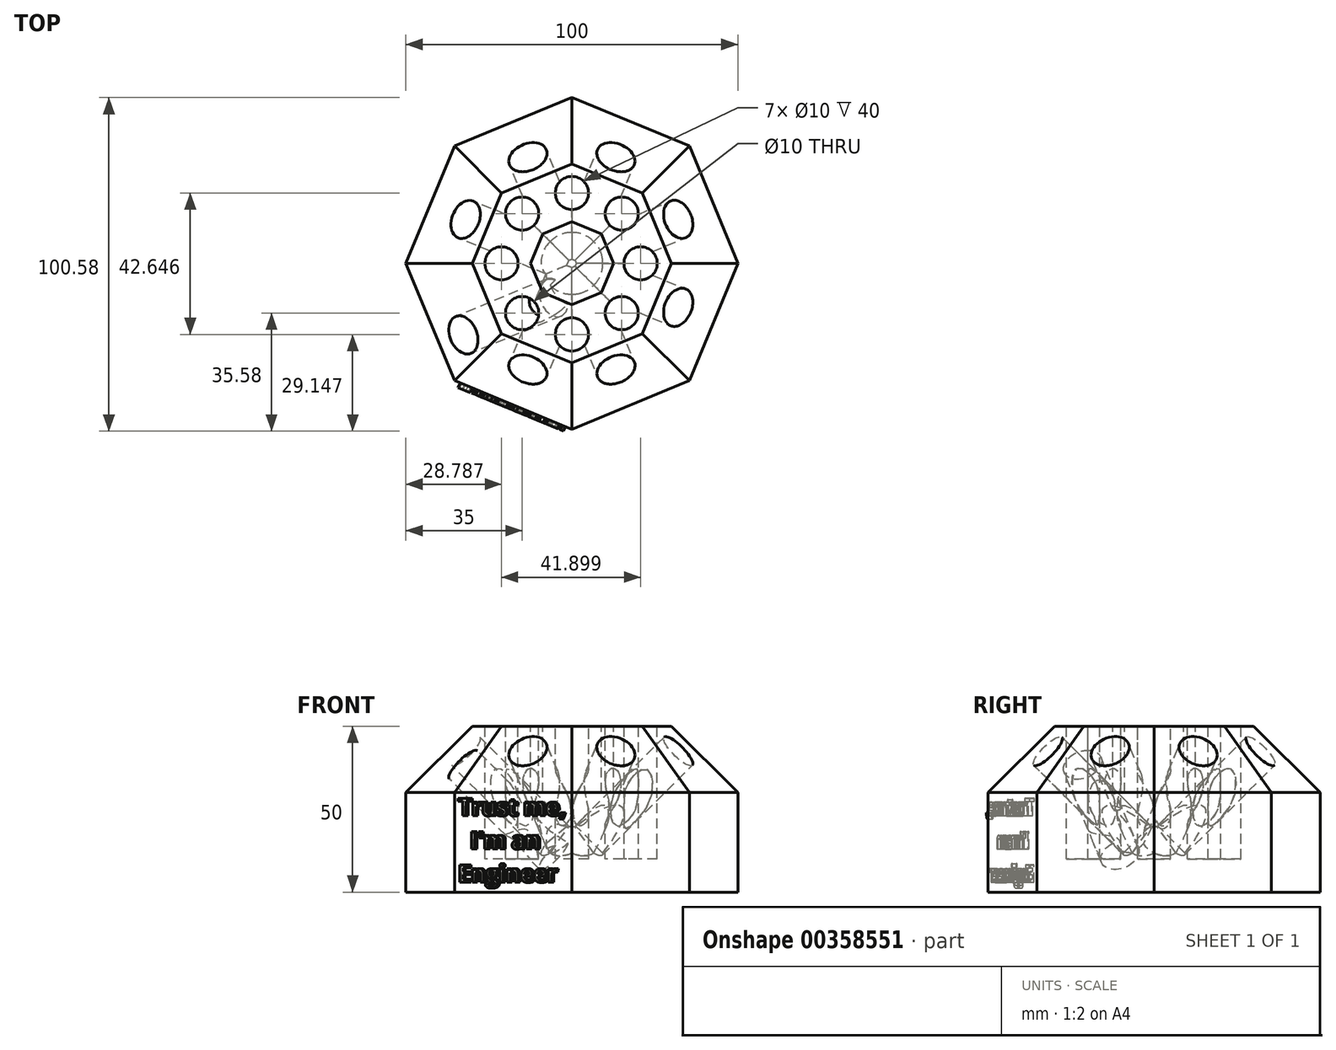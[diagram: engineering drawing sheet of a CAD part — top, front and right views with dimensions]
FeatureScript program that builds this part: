
annotation { "Feature Type Name" : "Feature", "Feature Type Description" : "" }
export const myFeature = defineFeature(function(context is Context, id is Id, definition is map)
    precondition{}
    {
        {
            var Q0;
            Q0=qCreatedBy(makeId("Top.planeOp"),FACE);
            var sketch = newSketch(context, id + "F0", { "sketchPlane" : qUnion([Q0])});
            skCircle(sketch, "E0.cCircle", {"center": v(0, 0) * mm, "radius": 50 * mm, "construction": true});
            skLineSegment(sketch, "E0.0", {"start": v(0, -50) * mm, "end": v(-35.36, -35.36) * mm});
            skLineSegment(sketch, "E0.1", {"start": v(-35.36, -35.36) * mm, "end": v(-50, 0) * mm});
            skLineSegment(sketch, "E0.2", {"start": v(-50, 0) * mm, "end": v(-35.36, 35.36) * mm});
            skLineSegment(sketch, "E0.3", {"start": v(-35.36, 35.36) * mm, "end": v(0, 50) * mm});
            skLineSegment(sketch, "E0.4", {"start": v(0, 50) * mm, "end": v(35.36, 35.36) * mm});
            skLineSegment(sketch, "E0.5", {"start": v(35.36, 35.36) * mm, "end": v(50, 0) * mm});
            skLineSegment(sketch, "E0.6", {"start": v(50, 0) * mm, "end": v(35.36, -35.36) * mm});
            skLineSegment(sketch, "E0.7", {"start": v(35.36, -35.36) * mm, "end": v(0, -50) * mm});
            skSolve(sketch);
        }
        {
            var Q0;
            Q0=makeQuery(id+"F0.imprint","IMPRINT",FACE,{"disambiguationData":[TD([[makeQuery(id+"F0.imprint","IMPRINT",EDGE,{"derivedFrom":sQuery(id+"F0.wireOp",EDGE,"E0.0")}),-1.0]])]});
            extrude(context, id + "F1", {"entities" : qUnion([Q0]), "depth" : 30 * mm});
        }
        {
            var Q0;
            Q0=makeQuery(id+"F1.opExtrude","CAP_FACE",FACE,{"disambiguationData":[OSD([sQuery(id+"F0.wireOp",EDGE,"E0.0"),sQuery(id+"F0.wireOp",EDGE,"E0.1"),sQuery(id+"F0.wireOp",EDGE,"E0.2"),sQuery(id+"F0.wireOp",EDGE,"E0.3"),sQuery(id+"F0.wireOp",EDGE,"E0.4"),sQuery(id+"F0.wireOp",EDGE,"E0.5"),sQuery(id+"F0.wireOp",EDGE,"E0.6"),sQuery(id+"F0.wireOp",EDGE,"E0.7")])],"isStart":false});
            cPlane(context, id + "F2", {"entities" : qUnion([Q0]), "cplaneType" : CPlaneType.OFFSET, "offset" : 20 * mm, "width" : 150 * mm, "height" : 150 * mm});
        }
        {
            var Q0;
            Q0=qCreatedBy(id+"F2.planeOp",FACE);
            var sketch = newSketch(context, id + "F3", { "sketchPlane" : qUnion([Q0])});
            skLineSegment(sketch, "E1.0.0", {"start": v(0, -50) * mm, "end": v(35.36, -35.36) * mm});
            skLineSegment(sketch, "E1.0.1", {"start": v(35.36, -35.36) * mm, "end": v(50, 0) * mm});
            skLineSegment(sketch, "E1.0.2", {"start": v(50, 0) * mm, "end": v(35.36, 35.36) * mm});
            skLineSegment(sketch, "E1.0.3", {"start": v(35.36, 35.36) * mm, "end": v(0, 50) * mm});
            skLineSegment(sketch, "E1.0.4", {"start": v(0, 50) * mm, "end": v(-35.36, 35.36) * mm});
            skLineSegment(sketch, "E1.0.5", {"start": v(-35.36, 35.36) * mm, "end": v(-50, 0) * mm});
            skLineSegment(sketch, "E1.0.6", {"start": v(-50, 0) * mm, "end": v(-35.36, -35.36) * mm});
            skLineSegment(sketch, "E1.0.7", {"start": v(-35.36, -35.36) * mm, "end": v(0, -50) * mm});
            skCircle(sketch, "E2.cCircle", {"center": v(0, 0) * mm, "radius": 30 * mm, "construction": true});
            skLineSegment(sketch, "E2.0", {"start": v(0, -30) * mm, "end": v(-21.21, -21.21) * mm});
            skLineSegment(sketch, "E2.1", {"start": v(-21.21, -21.21) * mm, "end": v(-30, 0) * mm});
            skLineSegment(sketch, "E2.2", {"start": v(-30, 0) * mm, "end": v(-21.21, 21.21) * mm});
            skLineSegment(sketch, "E2.3", {"start": v(-21.21, 21.21) * mm, "end": v(0, 30) * mm});
            skLineSegment(sketch, "E2.4", {"start": v(0, 30) * mm, "end": v(21.21, 21.21) * mm});
            skLineSegment(sketch, "E2.5", {"start": v(21.21, 21.21) * mm, "end": v(30, 0) * mm});
            skLineSegment(sketch, "E2.6", {"start": v(30, 0) * mm, "end": v(21.21, -21.21) * mm});
            skLineSegment(sketch, "E2.7", {"start": v(21.21, -21.21) * mm, "end": v(0, -30) * mm});
            skSolve(sketch);
        }
        {
            var Q1;
            Q1=makeQuery(id+"F1.opExtrude","CAP_FACE",FACE,{"disambiguationData":[OSD([sQuery(id+"F0.wireOp",EDGE,"E0.0"),sQuery(id+"F0.wireOp",EDGE,"E0.1"),sQuery(id+"F0.wireOp",EDGE,"E0.2"),sQuery(id+"F0.wireOp",EDGE,"E0.3"),sQuery(id+"F0.wireOp",EDGE,"E0.4"),sQuery(id+"F0.wireOp",EDGE,"E0.5"),sQuery(id+"F0.wireOp",EDGE,"E0.6"),sQuery(id+"F0.wireOp",EDGE,"E0.7")])],"isStart":false});
            var Q2;
            Q2=makeQuery(id+"F3.imprint","IMPRINT",FACE,{"disambiguationData":[TD([[makeQuery(id+"F3.imprint","IMPRINT",EDGE,{"derivedFrom":sQuery(id+"F3.wireOp",EDGE,"E2.0")}),-1.0]])]});
            loft(context, id + "F4", {"operationType" : NewBodyOperationType.ADD, "sheetProfilesArray" : [{ "sheetProfileEntities" : qUnion([Q1]) }, { "sheetProfileEntities" : qUnion([Q2]) }]});
        }
        {
            var Q0;
            Q0=makeQuery(id+"F4.opLoft","SWEPT_FACE",FACE,{"disambiguationData":[OSD([sQuery(id+"F0.wireOp",EDGE,"E0.0"),sQuery(id+"F0.wireOp",EDGE,"E0.1"),sQuery(id+"F0.wireOp",EDGE,"E0.2"),sQuery(id+"F3.wireOp",EDGE,"E2.0"),sQuery(id+"F3.wireOp",EDGE,"E2.1"),sQuery(id+"F3.wireOp",EDGE,"E2.2")])]});
            var sketch = newSketch(context, id + "F5", { "sketchPlane" : qUnion([Q0])});
            skLineSegment(sketch, "E3", {"start": v(9.31, 19.13) * mm, "end": v(2.02, -21.18) * mm, "construction": true});
            skLineSegment(sketch, "E4", {"start": v(-17.92, 11.48) * mm, "end": v(21.27, -0.46) * mm, "construction": true});
            skCircle(sketch, "E5", {"center": v(6.58, 4.02) * mm, "radius": 6 * mm});
            skSolve(sketch);
        }
        {
            var Q0;
            Q0=makeQuery(id+"F5.imprint","IMPRINT",FACE,{"disambiguationData":[TD([[makeQuery(id+"F5.imprint","IMPRINT",EDGE,{"derivedFrom":sQuery(id+"F5.wireOp",EDGE,"E5")}),1.0]])]});
            extrude(context, id + "F6", {"entities" : qUnion([Q0]), "operationType" : NewBodyOperationType.REMOVE, "oppositeDirection" : true, "depth" : 40 * mm});
        }
        {
            var Q0;
            Q0=makeQuery(id+"F4.opLoft","SWEPT_FACE",FACE,{"disambiguationData":[OSD([sQuery(id+"F0.wireOp",EDGE,"E0.0"),sQuery(id+"F0.wireOp",EDGE,"E0.1"),sQuery(id+"F0.wireOp",EDGE,"E0.7"),sQuery(id+"F3.wireOp",EDGE,"E2.0"),sQuery(id+"F3.wireOp",EDGE,"E2.1"),sQuery(id+"F3.wireOp",EDGE,"E2.7")])]});
            var sketch = newSketch(context, id + "F7", { "sketchPlane" : qUnion([Q0])});
            skLineSegment(sketch, "E6", {"start": v(-6.2, 20.36) * mm, "end": v(15.9, -14.14) * mm, "construction": true});
            skLineSegment(sketch, "E7", {"start": v(15.9, 14.14) * mm, "end": v(-20.94, -3.79) * mm, "construction": true});
            skCircle(sketch, "E8", {"center": v(2.09, 7.42) * mm, "radius": 6 * mm});
            skSolve(sketch);
        }
        {
            var Q0;
            Q0=makeQuery(id+"F7.imprint","IMPRINT",FACE,{"disambiguationData":[TD([[makeQuery(id+"F7.imprint","IMPRINT",EDGE,{"derivedFrom":sQuery(id+"F7.wireOp",EDGE,"E8")}),1.0]])]});
            extrude(context, id + "F8", {"entities" : qUnion([Q0]), "operationType" : NewBodyOperationType.REMOVE, "oppositeDirection" : true, "depth" : 40 * mm});
        }
        {
            var Q0;
            Q0=makeQuery(id+"F4.opLoft","SWEPT_FACE",FACE,{"disambiguationData":[OSD([sQuery(id+"F0.wireOp",EDGE,"E0.0"),sQuery(id+"F0.wireOp",EDGE,"E0.6"),sQuery(id+"F0.wireOp",EDGE,"E0.7"),sQuery(id+"F3.wireOp",EDGE,"E2.0"),sQuery(id+"F3.wireOp",EDGE,"E2.6"),sQuery(id+"F3.wireOp",EDGE,"E2.7")])]});
            var sketch = newSketch(context, id + "F9", { "sketchPlane" : qUnion([Q0])});
            skLineSegment(sketch, "E9", {"start": v(20.94, -3.79) * mm, "end": v(-15.9, 14.14) * mm, "construction": true});
            skLineSegment(sketch, "E10", {"start": v(-15.9, -14.14) * mm, "end": v(6.2, 20.36) * mm, "construction": true});
            skCircle(sketch, "E11", {"center": v(-2.09, 7.42) * mm, "radius": 6 * mm});
            skSolve(sketch);
        }
        {
            var Q0;
            Q0=makeQuery(id+"F4.opLoft","SWEPT_FACE",FACE,{"disambiguationData":[OSD([sQuery(id+"F0.wireOp",EDGE,"E0.5"),sQuery(id+"F0.wireOp",EDGE,"E0.6"),sQuery(id+"F0.wireOp",EDGE,"E0.7"),sQuery(id+"F3.wireOp",EDGE,"E2.5"),sQuery(id+"F3.wireOp",EDGE,"E2.6"),sQuery(id+"F3.wireOp",EDGE,"E2.7")])]});
            var sketch = newSketch(context, id + "F10", { "sketchPlane" : qUnion([Q0])});
            skLineSegment(sketch, "E12", {"start": v(-20.94, -3.79) * mm, "end": v(15.9, 14.14) * mm, "construction": true});
            skLineSegment(sketch, "E13", {"start": v(-6.2, 20.36) * mm, "end": v(15.9, -14.14) * mm, "construction": true});
            skCircle(sketch, "E14", {"center": v(2.09, 7.42) * mm, "radius": 6 * mm});
            skSolve(sketch);
        }
        {
            var Q0;
            Q0=makeQuery(id+"F4.opLoft","SWEPT_FACE",FACE,{"disambiguationData":[OSD([sQuery(id+"F0.wireOp",EDGE,"E0.4"),sQuery(id+"F0.wireOp",EDGE,"E0.5"),sQuery(id+"F0.wireOp",EDGE,"E0.6"),sQuery(id+"F3.wireOp",EDGE,"E2.4"),sQuery(id+"F3.wireOp",EDGE,"E2.5"),sQuery(id+"F3.wireOp",EDGE,"E2.6")])]});
            var sketch = newSketch(context, id + "F11", { "sketchPlane" : qUnion([Q0])});
            skLineSegment(sketch, "E15", {"start": v(-15.9, -14.14) * mm, "end": v(6.2, 20.36) * mm, "construction": true});
            skLineSegment(sketch, "E16", {"start": v(-15.9, 14.14) * mm, "end": v(20.94, -3.79) * mm, "construction": true});
            skCircle(sketch, "E17", {"center": v(-2.09, 7.42) * mm, "radius": 6 * mm});
            skSolve(sketch);
        }
        {
            var Q0;
            Q0=makeQuery(id+"F4.opLoft","SWEPT_FACE",FACE,{"disambiguationData":[OSD([sQuery(id+"F0.wireOp",EDGE,"E0.3"),sQuery(id+"F0.wireOp",EDGE,"E0.4"),sQuery(id+"F0.wireOp",EDGE,"E0.5"),sQuery(id+"F3.wireOp",EDGE,"E2.3"),sQuery(id+"F3.wireOp",EDGE,"E2.4"),sQuery(id+"F3.wireOp",EDGE,"E2.5")])]});
            var sketch = newSketch(context, id + "F12", { "sketchPlane" : qUnion([Q0])});
            skLineSegment(sketch, "E18", {"start": v(-6.2, 20.36) * mm, "end": v(15.9, -14.14) * mm, "construction": true});
            skLineSegment(sketch, "E19", {"start": v(15.9, 14.14) * mm, "end": v(-20.94, -3.79) * mm, "construction": true});
            skCircle(sketch, "E20", {"center": v(2.09, 7.42) * mm, "radius": 6 * mm});
            skSolve(sketch);
        }
        {
            var Q0;
            Q0=makeQuery(id+"F4.opLoft","SWEPT_FACE",FACE,{"disambiguationData":[OSD([sQuery(id+"F0.wireOp",EDGE,"E0.2"),sQuery(id+"F0.wireOp",EDGE,"E0.3"),sQuery(id+"F0.wireOp",EDGE,"E0.4"),sQuery(id+"F3.wireOp",EDGE,"E2.2"),sQuery(id+"F3.wireOp",EDGE,"E2.3"),sQuery(id+"F3.wireOp",EDGE,"E2.4")])]});
            var sketch = newSketch(context, id + "F13", { "sketchPlane" : qUnion([Q0])});
            skLineSegment(sketch, "E21", {"start": v(-15.9, 14.14) * mm, "end": v(20.94, -3.79) * mm, "construction": true});
            skLineSegment(sketch, "E22", {"start": v(6.2, 20.36) * mm, "end": v(-15.9, -14.14) * mm, "construction": true});
            skCircle(sketch, "E23", {"center": v(-2.09, 7.42) * mm, "radius": 6 * mm});
            skSolve(sketch);
        }
        {
            var Q0;
            Q0=makeQuery(id+"F4.opLoft","SWEPT_FACE",FACE,{"disambiguationData":[OSD([sQuery(id+"F0.wireOp",EDGE,"E0.1"),sQuery(id+"F0.wireOp",EDGE,"E0.2"),sQuery(id+"F0.wireOp",EDGE,"E0.3"),sQuery(id+"F3.wireOp",EDGE,"E2.1"),sQuery(id+"F3.wireOp",EDGE,"E2.2"),sQuery(id+"F3.wireOp",EDGE,"E2.3")])]});
            var sketch = newSketch(context, id + "F14", { "sketchPlane" : qUnion([Q0])});
            skLineSegment(sketch, "E24", {"start": v(15.9, 14.14) * mm, "end": v(-20.94, -3.79) * mm, "construction": true});
            skLineSegment(sketch, "E25", {"start": v(-6.2, 20.36) * mm, "end": v(15.9, -14.14) * mm, "construction": true});
            skCircle(sketch, "E26", {"center": v(2.09, 7.42) * mm, "radius": 6 * mm});
            skSolve(sketch);
        }
        {
            var Q0;
            Q0=makeQuery(id+"F9.imprint","IMPRINT",FACE,{"disambiguationData":[TD([[makeQuery(id+"F9.imprint","IMPRINT",EDGE,{"derivedFrom":sQuery(id+"F9.wireOp",EDGE,"E11")}),1.0]])]});
            extrude(context, id + "F15", {"entities" : qUnion([Q0]), "operationType" : NewBodyOperationType.REMOVE, "oppositeDirection" : true, "depth" : 40 * mm});
        }
        {
            var Q0;
            Q0=makeQuery(id+"F10.imprint","IMPRINT",FACE,{"disambiguationData":[TD([[makeQuery(id+"F10.imprint","IMPRINT",EDGE,{"derivedFrom":sQuery(id+"F10.wireOp",EDGE,"E14")}),1.0]])]});
            extrude(context, id + "F16", {"entities" : qUnion([Q0]), "operationType" : NewBodyOperationType.REMOVE, "oppositeDirection" : true, "depth" : 40 * mm});
        }
        {
            var Q0;
            Q0=makeQuery(id+"F11.imprint","IMPRINT",FACE,{"disambiguationData":[TD([[makeQuery(id+"F11.imprint","IMPRINT",EDGE,{"derivedFrom":sQuery(id+"F11.wireOp",EDGE,"E17")}),1.0]])]});
            extrude(context, id + "F17", {"entities" : qUnion([Q0]), "operationType" : NewBodyOperationType.REMOVE, "oppositeDirection" : true, "depth" : 40 * mm});
        }
        {
            var Q0;
            Q0=makeQuery(id+"F12.imprint","IMPRINT",FACE,{"disambiguationData":[TD([[makeQuery(id+"F12.imprint","IMPRINT",EDGE,{"derivedFrom":sQuery(id+"F12.wireOp",EDGE,"E20")}),1.0]])]});
            extrude(context, id + "F18", {"entities" : qUnion([Q0]), "operationType" : NewBodyOperationType.REMOVE, "oppositeDirection" : true, "depth" : 40 * mm});
        }
        {
            var Q0;
            Q0=makeQuery(id+"F13.imprint","IMPRINT",FACE,{"disambiguationData":[TD([[makeQuery(id+"F13.imprint","IMPRINT",EDGE,{"derivedFrom":sQuery(id+"F13.wireOp",EDGE,"E23")}),1.0]])]});
            extrude(context, id + "F19", {"entities" : qUnion([Q0]), "operationType" : NewBodyOperationType.REMOVE, "oppositeDirection" : true, "depth" : 40 * mm});
        }
        {
            var Q0;
            Q0=makeQuery(id+"F14.imprint","IMPRINT",FACE,{"disambiguationData":[TD([[makeQuery(id+"F14.imprint","IMPRINT",EDGE,{"derivedFrom":sQuery(id+"F14.wireOp",EDGE,"E26")}),1.0]])]});
            extrude(context, id + "F20", {"entities" : qUnion([Q0]), "operationType" : NewBodyOperationType.REMOVE, "oppositeDirection" : true, "depth" : 40 * mm});
        }
        {
            var Q0;
            Q0=makeQuery(id+"F4.opLoft","CAP_FACE",FACE,{"disambiguationData":[OSD([makeQuery(id+"F3.imprint","IMPRINT",FACE,{"disambiguationData":[TD([[makeQuery(id+"F3.imprint","IMPRINT",EDGE,{"derivedFrom":sQuery(id+"F3.wireOp",EDGE,"E2.0")}),-1.0]])]})])],"isStart":true});
            var sketch = newSketch(context, id + "F21", { "sketchPlane" : qUnion([Q0])});
            skLineSegment(sketch, "E27", {"start": v(0, 30) * mm, "end": v(0, -30) * mm, "construction": true});
            skLineSegment(sketch, "E28", {"start": v(-21.21, -21.21) * mm, "end": v(21.21, 21.21) * mm, "construction": true});
            skLineSegment(sketch, "E29", {"start": v(-21.21, 21.21) * mm, "end": v(21.21, -21.21) * mm, "construction": true});
            skLineSegment(sketch, "E30", {"start": v(21.21, -21.21) * mm, "end": v(20.15, -21.64) * mm, "construction": true});
            skLineSegment(sketch, "E31", {"start": v(-30, 0) * mm, "end": v(30, 0) * mm, "construction": true});
            skLineSegment(sketch, "E32", {"start": v(-21.21, -21.21) * mm, "end": v(-21.21, 21.21) * mm, "construction": true});
            skLineSegment(sketch, "E33", {"start": v(21.21, 21.21) * mm, "end": v(-21.21, 21.21) * mm, "construction": true});
            skLineSegment(sketch, "E34", {"start": v(-21.21, -21.21) * mm, "end": v(20.15, -21.64) * mm, "construction": true});
            skLineSegment(sketch, "E35", {"start": v(20.15, -21.64) * mm, "end": v(21.21, 21.21) * mm, "construction": true});
            skLineSegment(sketch, "E36", {"start": v(-30, 0) * mm, "end": v(0, 30) * mm, "construction": true});
            skLineSegment(sketch, "E37", {"start": v(0, 30) * mm, "end": v(30, 0) * mm, "construction": true});
            skLineSegment(sketch, "E38", {"start": v(30, 0) * mm, "end": v(0, -30) * mm, "construction": true});
            skLineSegment(sketch, "E39", {"start": v(0, -30) * mm, "end": v(-30, 0) * mm, "construction": true});
            skCircle(sketch, "E40", {"center": v(-15, 15) * mm, "radius": 5 * mm});
            skCircle(sketch, "E41", {"center": v(0, 21.21) * mm, "radius": 5 * mm});
            skCircle(sketch, "E42", {"center": v(-21.21, 0) * mm, "radius": 5 * mm});
            skCircle(sketch, "E43", {"center": v(-15, -15) * mm, "radius": 5 * mm});
            skCircle(sketch, "E44", {"center": v(0, -21.43) * mm, "radius": 5 * mm});
            skCircle(sketch, "E45", {"center": v(15, -15) * mm, "radius": 5 * mm});
            skCircle(sketch, "E46", {"center": v(20.69, 0) * mm, "radius": 5 * mm});
            skCircle(sketch, "E47", {"center": v(15, 15) * mm, "radius": 5 * mm});
            skCircle(sketch, "E48.cCircle", {"center": v(0, 0) * mm, "radius": 12.5 * mm, "construction": true});
            skLineSegment(sketch, "E48.0", {"start": v(-12.5, 0) * mm, "end": v(-8.84, 8.84) * mm});
            skLineSegment(sketch, "E48.1", {"start": v(-8.84, 8.84) * mm, "end": v(0, 12.5) * mm});
            skLineSegment(sketch, "E48.2", {"start": v(0, 12.5) * mm, "end": v(8.84, 8.84) * mm});
            skLineSegment(sketch, "E48.3", {"start": v(8.84, 8.84) * mm, "end": v(12.5, 0) * mm});
            skLineSegment(sketch, "E48.4", {"start": v(12.5, 0) * mm, "end": v(8.84, -8.84) * mm});
            skLineSegment(sketch, "E48.5", {"start": v(8.84, -8.84) * mm, "end": v(0, -12.5) * mm});
            skLineSegment(sketch, "E48.6", {"start": v(0, -12.5) * mm, "end": v(-8.84, -8.84) * mm});
            skLineSegment(sketch, "E48.7", {"start": v(-8.84, -8.84) * mm, "end": v(-12.5, 0) * mm});
            skSolve(sketch);
        }
        {
            var Q0;
            Q0=makeQuery(id+"F21.imprint","IMPRINT",FACE,{"disambiguationData":[TD([[makeQuery(id+"F21.imprint","IMPRINT",EDGE,{"derivedFrom":sQuery(id+"F21.wireOp",EDGE,"E41")}),1.0]])]});
            var Q1;
            Q1=makeQuery(id+"F21.imprint","IMPRINT",FACE,{"disambiguationData":[TD([[makeQuery(id+"F21.imprint","IMPRINT",EDGE,{"derivedFrom":sQuery(id+"F21.wireOp",EDGE,"E40")}),1.0]])]});
            var Q2;
            Q2=makeQuery(id+"F21.imprint","IMPRINT",FACE,{"disambiguationData":[TD([[makeQuery(id+"F21.imprint","IMPRINT",EDGE,{"derivedFrom":sQuery(id+"F21.wireOp",EDGE,"E42")}),1.0]])]});
            var Q3;
            Q3=makeQuery(id+"F21.imprint","IMPRINT",FACE,{"disambiguationData":[TD([[makeQuery(id+"F21.imprint","IMPRINT",EDGE,{"derivedFrom":sQuery(id+"F21.wireOp",EDGE,"E43")}),1.0]])]});
            var Q4;
            Q4=makeQuery(id+"F21.imprint","IMPRINT",FACE,{"disambiguationData":[TD([[makeQuery(id+"F21.imprint","IMPRINT",EDGE,{"derivedFrom":sQuery(id+"F21.wireOp",EDGE,"E44")}),1.0]])]});
            var Q5;
            Q5=makeQuery(id+"F21.imprint","IMPRINT",FACE,{"disambiguationData":[TD([[makeQuery(id+"F21.imprint","IMPRINT",EDGE,{"derivedFrom":sQuery(id+"F21.wireOp",EDGE,"E45")}),1.0]])]});
            var Q6;
            Q6=makeQuery(id+"F21.imprint","IMPRINT",FACE,{"disambiguationData":[TD([[makeQuery(id+"F21.imprint","IMPRINT",EDGE,{"derivedFrom":sQuery(id+"F21.wireOp",EDGE,"E46")}),1.0]])]});
            var Q7;
            Q7=makeQuery(id+"F21.imprint","IMPRINT",FACE,{"disambiguationData":[TD([[makeQuery(id+"F21.imprint","IMPRINT",EDGE,{"derivedFrom":sQuery(id+"F21.wireOp",EDGE,"E47")}),1.0]])]});
            extrude(context, id + "F22", {"entities" : qUnion([Q0, Q1, Q2, Q3, Q4, Q5, Q6, Q7]), "operationType" : NewBodyOperationType.REMOVE, "oppositeDirection" : true, "depth" : 40 * mm});
        }
        {
            var Q0;
            Q0=makeQuery(id+"F21.imprint","IMPRINT",FACE,{"disambiguationData":[TD([[makeQuery(id+"F21.imprint","IMPRINT",EDGE,{"derivedFrom":sQuery(id+"F21.wireOp",EDGE,"E48.0")}),-1.0]])]});
            extrude(context, id + "F23", {"entities" : qUnion([Q0]), "operationType" : NewBodyOperationType.REMOVE, "oppositeDirection" : true, "depth" : 20 * mm});
        }
        {
            var Q0;
            Q0=makeQuery(id+"F1.opExtrude","SWEPT_FACE",FACE,{"disambiguationData":[OSD([sQuery(id+"F0.wireOp",EDGE,"E0.0")])]});
            var sketch = newSketch(context, id + "F24", { "sketchPlane" : qUnion([Q0])});
            skText(sketch, "E49", { "text": "Trust me, \n  I\'m an \nEngineer", "fontName": "OpenSans-Bold.ttf"});
            const initialGuessF24  = {"E49": [-0.01746, 0.02304, 1, 0, 0.00531]};
            skSetInitialGuess(sketch, initialGuessF24);
            skSolve(sketch);
        }
        {
            var Q0;
            Q0 = qSketchRegion(id + "F24", true);
            extrude(context, id + "F25", {"entities" : qUnion([Q0]), "operationType" : NewBodyOperationType.ADD, "depth" : 1.5 * mm});
        }
    });
